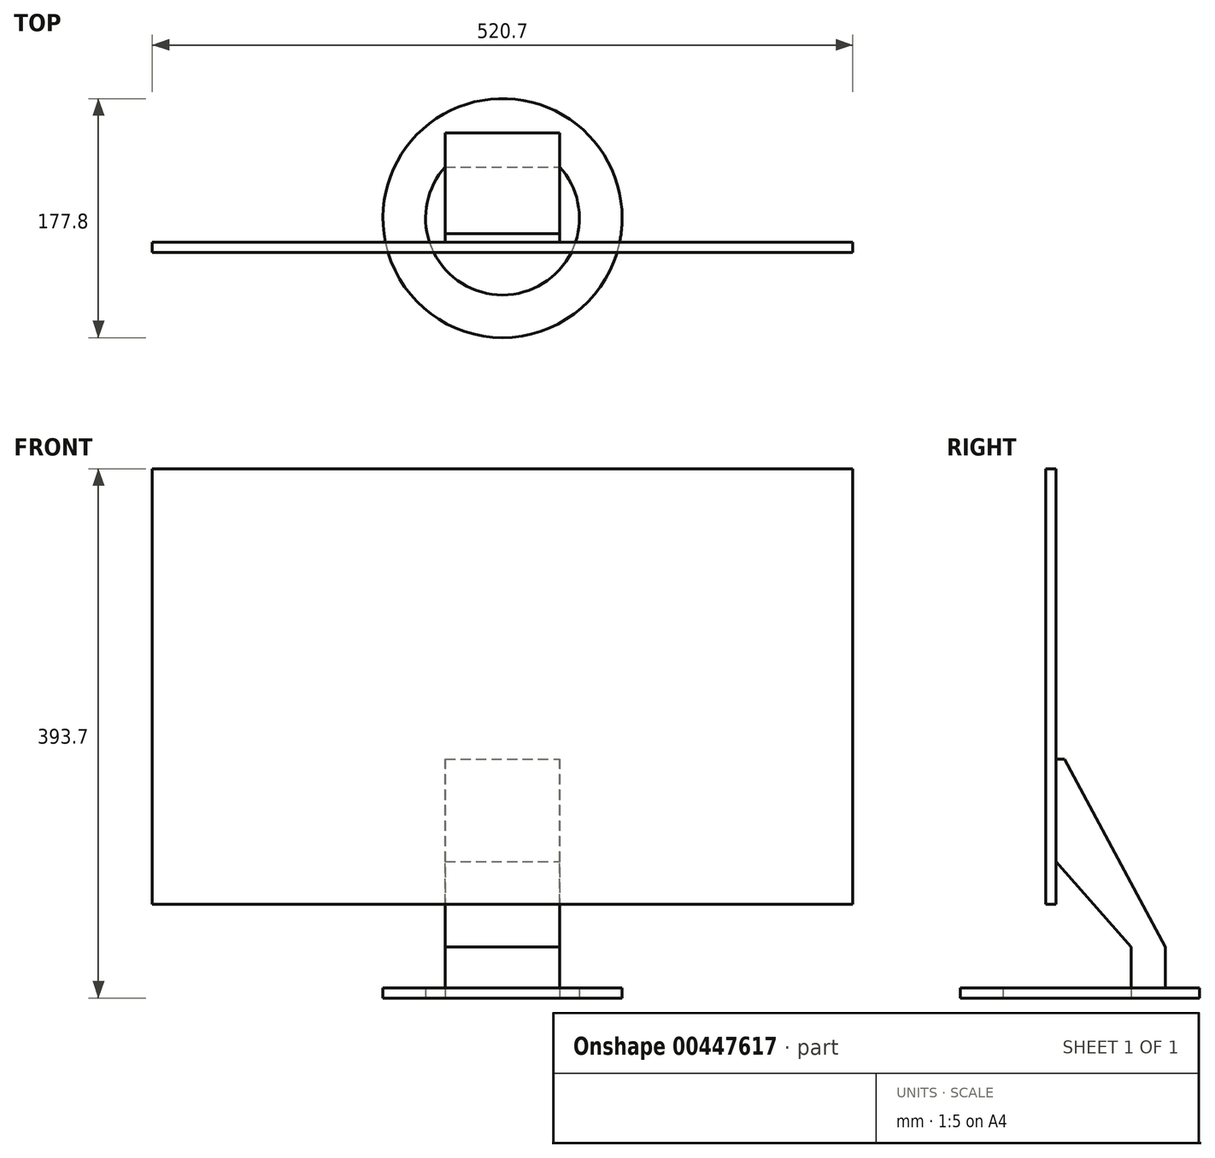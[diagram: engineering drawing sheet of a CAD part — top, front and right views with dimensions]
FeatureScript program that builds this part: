
annotation { "Feature Type Name" : "Feature", "Feature Type Description" : "" }
export const myFeature = defineFeature(function(context is Context, id is Id, definition is map)
    precondition{}
    {
        {
            var Q0;
            Q0=qCreatedBy(makeId("Front.planeOp"),FACE);
            var sketch = newSketch(context, id + "F0", { "sketchPlane" : qUnion([Q0])});
            skLineSegment(sketch, "E0.bottom", {"start": v(0, 0) * mm, "end": v(520.7, 0) * mm});
            skLineSegment(sketch, "E0.top", {"start": v(0, 323.85) * mm, "end": v(520.7, 323.85) * mm});
            skLineSegment(sketch, "E0.left", {"start": v(0, 0) * mm, "end": v(0, 323.85) * mm});
            skLineSegment(sketch, "E0.right", {"start": v(520.7, 0) * mm, "end": v(520.7, 323.85) * mm});
            skSolve(sketch);
        }
        {
            var Q0;
            Q0 = qSketchRegion(id + "F0", true);
            extrude(context, id + "F1", {"entities" : qUnion([Q0]), "oppositeDirection" : true, "depth" : 7.62 * mm});
        }
        {
            var Q0;
            Q0=qCreatedBy(makeId("Top.planeOp"),FACE);
            cPlane(context, id + "F2", {"entities" : qUnion([Q0]), "cplaneType" : CPlaneType.OFFSET, "offset" : 69.85 * mm, "oppositeDirection" : true, "width" : 152.4 * mm, "height" : 152.4 * mm});
        }
        {
            var Q0;
            Q0=qCreatedBy(id+"F2.planeOp",FACE);
            var sketch = newSketch(context, id + "F3", { "sketchPlane" : qUnion([Q0])});
            skCircle(sketch, "E1", {"center": v(260.35, 25.4) * mm, "radius": 88.9 * mm});
            skLineSegment(sketch, "E2", {"start": v(0, 0) * mm, "end": v(520.7, 0) * mm, "construction": true});
            skLineSegment(sketch, "E3", {"start": v(260.35, 25.4) * mm, "end": v(260.35, 0) * mm, "construction": true});
            skCircle(sketch, "E4.0", {"center": v(260.35, 25.4) * mm, "radius": 57.15 * mm});
            skSolve(sketch);
        }
        {
            var Q0;
            Q0 = qSketchRegion(id + "F3", true);
            extrude(context, id + "F4", {"entities" : qUnion([Q0]), "depth" : 7.62 * mm});
        }
        {
            var Q0;
            Q0=qCreatedBy(id+"F2.planeOp",FACE);
            var sketch = newSketch(context, id + "F5", { "sketchPlane" : qUnion([Q0])});
            skCircle(sketch, "E5.0", {"center": v(260.35, 25.4) * mm, "radius": 57.15 * mm, "construction": true});
            skLineSegment(sketch, "E6.bottom", {"start": v(217.75, 63.5) * mm, "end": v(302.95, 63.5) * mm});
            skLineSegment(sketch, "E6.top", {"start": v(217.75, 88.9) * mm, "end": v(302.95, 88.9) * mm});
            skLineSegment(sketch, "E6.left", {"start": v(217.75, 63.5) * mm, "end": v(217.75, 88.9) * mm});
            skLineSegment(sketch, "E6.right", {"start": v(302.95, 63.5) * mm, "end": v(302.95, 88.9) * mm});
            skLineSegment(sketch, "E7", {"start": v(260.35, 63.5) * mm, "end": v(260.35, 88.9) * mm, "construction": true});
            skLineSegment(sketch, "E8", {"start": v(260.35, 25.4) * mm, "end": v(260.35, 63.5) * mm, "construction": true});
            skSolve(sketch);
        }
        {
            var Q0;
            Q0 = qSketchRegion(id + "F5", true);
            extrude(context, id + "F6", {"entities" : qUnion([Q0]), "operationType" : NewBodyOperationType.ADD, "depth" : 38.1 * mm});
        }
        {
            var Q0;
            Q0=makeQuery(id+"F6.opExtrude","SWEPT_FACE",FACE,{"disambiguationData":[OSD([sQuery(id+"F5.wireOp",EDGE,"E6.right")])]});
            var sketch = newSketch(context, id + "F7", { "sketchPlane" : qUnion([Q0])});
            skLineSegment(sketch, "E9", {"start": v(63.5, -31.75) * mm, "end": v(7.62, 31.75) * mm});
            skLineSegment(sketch, "E10", {"start": v(7.62, 31.75) * mm, "end": v(7.62, 107.95) * mm});
            skLineSegment(sketch, "E11", {"start": v(7.62, 107.95) * mm, "end": v(13.97, 107.95) * mm});
            skLineSegment(sketch, "E12", {"start": v(13.97, 107.95) * mm, "end": v(88.9, -31.75) * mm});
            skLineSegment(sketch, "E13", {"start": v(88.9, -31.75) * mm, "end": v(63.5, -31.75) * mm});
            skLineSegment(sketch, "E14.0", {"start": v(7.62, 0) * mm, "end": v(7.62, 323.85) * mm, "construction": true});
            skSolve(sketch);
        }
        {
            var Q0;
            Q0 = qSketchRegion(id + "F7", true);
            var Q1;
            Q1=makeQuery(id+"F6.opExtrude","SWEPT_FACE",FACE,{"disambiguationData":[OSD([sQuery(id+"F5.wireOp",EDGE,"E6.left")])]});
            extrude(context, id + "F8", {"entities" : qUnion([Q0]), "operationType" : NewBodyOperationType.ADD, "endBound" : BoundingType.UP_TO_SURFACE, "oppositeDirection" : true, "endBoundEntityFace" : qUnion([Q1]), "depth" : 25.4 * mm});
        }
    });
